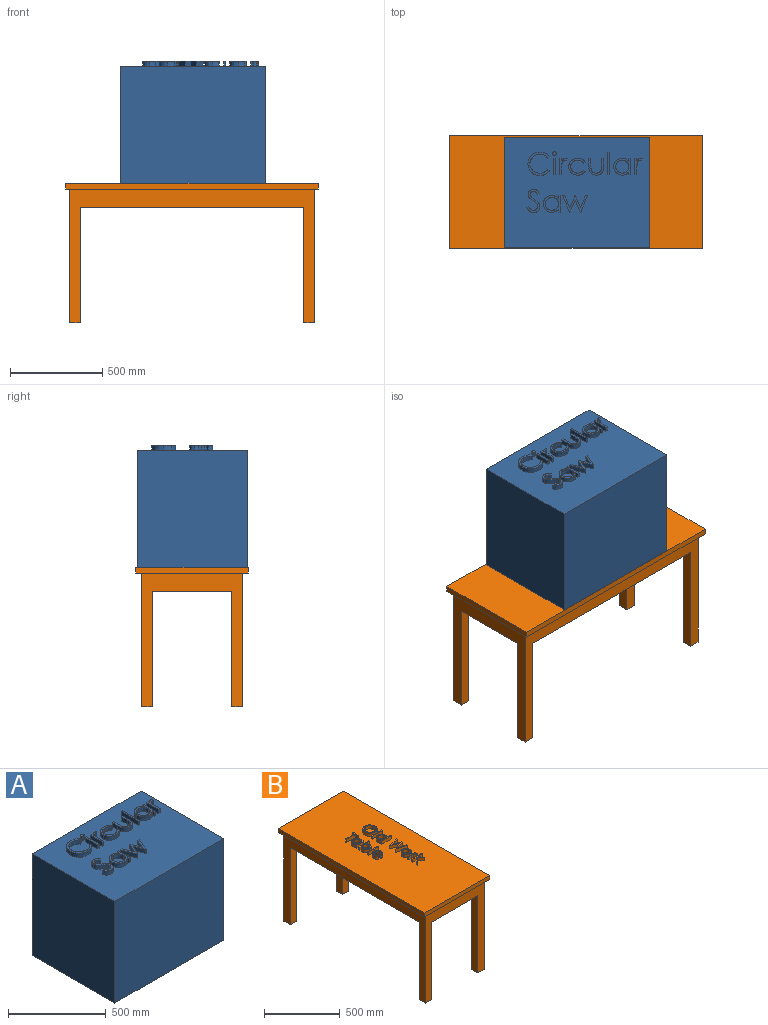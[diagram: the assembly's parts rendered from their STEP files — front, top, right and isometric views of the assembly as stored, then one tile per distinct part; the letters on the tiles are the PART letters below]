
ASSEMBLY  parts=2 mates=1
PART A: 143 faces, bbox 787.4x596.9x660.4 mm
  f0: plane 787.4x596.9mm, normal (0,0,1), area 436057.9mm2, adj f1,f2,f3,f4,f6,f7,f8,f9
  f1: plane 635x596.9mm, normal (-1,0,0), area 379031.5mm2, adj f0,f2,f4,f5
  f2: plane 787.4x635mm, normal (0,-1,0), area 499999mm2, adj f0,f1,f3,f5
  f3: plane 635x596.9mm, normal (1,0,0), area 379031.5mm2, adj f0,f2,f4,f5
  f4: plane 787.4x635mm, normal (0,1,0), area 499999mm2, adj f0,f1,f3,f5
  f5: plane 787.4x596.9mm, normal (0,0,-1), area 469999.1mm2, adj f1,f2,f3,f4
  f6: extruded ~52.64x25.4mm, area 1541mm2, adj f0,f7,f16,f17
  f7: extruded ~64.92x62.72mm, area 2561.4mm2, adj f0,f6,f8,f17
  f8: extruded ~43.02x25.4mm, area 1185.6mm2, adj f0,f7,f9,f17
  f9: extruded ~49.76x25.4mm, area 1419.2mm2, adj f0,f8,f10,f17
  f10: extruded ~52.49x25.4mm, area 1537.6mm2, adj f0,f9,f11,f17
  f11: plane 25.4x9.47mm, normal (0.6,0.8,0), area 301.9mm2, adj f0,f10,f12,f17
  f12: extruded ~43.09x25.4mm, area 1248.8mm2, adj f0,f11,f13,f17
  f13: extruded ~54.16x50.92mm, area 2112.1mm2, adj f0,f12,f14,f17
  f14: extruded ~53.41x51.17mm, area 2096.1mm2, adj f0,f13,f15,f17
  f15: extruded ~43.84x25.4mm, area 1268.5mm2, adj f0,f14,f16,f17
  f16: plane 25.4x9.47mm, normal (0.61,-0.79,0), area 303mm2, adj f0,f6,f15,f17
  f17: plane 126.84x117.56mm, normal (0,0,1), area 3542.4mm2, adj f6,f7,f8,f9,f10,f11,f12,f13
  f18: extruded ~25.4x10.01mm, area 386mm2, adj f0,f19,f21,f22
  f19: extruded ~25.4x10.01mm, area 383.7mm2, adj f0,f18,f20,f22
  f20: extruded ~25.4x10.1mm, area 385.9mm2, adj f0,f19,f21,f22
  f21: extruded ~25.4x10.1mm, area 388.2mm2, adj f0,f18,f20,f22
  f22: plane 20.11x18.56mm, normal (0,0,1), area 293.2mm2, adj f18,f19,f20,f21
  f23: plane 88.17x25.4mm, normal (-1,0,0), area 2239.4mm2, adj f0,f24,f26,f27
  f24: plane 25.4x10.83mm, normal (0,-1,0), area 275mm2, adj f0,f23,f25,f27
  f25: plane 88.17x25.4mm, normal (1,0,0), area 2239.4mm2, adj f0,f24,f26,f27
  f26: plane 25.4x10.83mm, normal (0,1,0), area 275mm2, adj f0,f23,f25,f27
  f27: plane 88.17x10.83mm, normal (0,0,1), area 954.6mm2, adj f23,f24,f25,f26
  f28: plane 88.17x25.4mm, normal (-1,0,0), area 2239.4mm2, adj f0,f29,f38,f39
  f29: plane 25.4x10.83mm, normal (0,-1,0), area 275mm2, adj f0,f28,f30,f39
  f30: plane 29.63x25.4mm, normal (1,0,0), area 752.6mm2, adj f0,f29,f31,f39
  f31: extruded ~30.26x25.4mm, area 771.6mm2, adj f0,f30,f32,f39
  f32: extruded ~25.4x19mm, area 705.1mm2, adj f0,f31,f33,f39
  f33: extruded ~25.4x5.53mm, area 147.3mm2, adj f0,f32,f34,f39
  f34: plane 25.4x9.38mm, normal (0.84,-0.54,0), area 282mm2, adj f0,f33,f35,f39
  f35: extruded ~25.4x9.43mm, area 254.5mm2, adj f0,f34,f36,f39
  f36: extruded ~25.4x21.51mm, area 689.8mm2, adj f0,f35,f37,f39
  f37: plane 25.4x12.98mm, normal (1,0,0), area 329.7mm2, adj f0,f36,f38,f39
  f38: plane 25.4x10.83mm, normal (0,1,0), area 275mm2, adj f0,f28,f37,f39
  f39: plane 89.71x41.76mm, normal (0,0,1), area 1310.5mm2, adj f28,f29,f30,f31,f32,f33,f34,f35
  f40: extruded ~40.36x25.4mm, area 1205.3mm2, adj f0,f41,f49,f50
  f41: extruded ~49.35x46.36mm, area 1919.1mm2, adj f0,f40,f42,f50
  f42: extruded ~48.46x44.91mm, area 1873mm2, adj f0,f41,f43,f50
  f43: extruded ~41.26x25.4mm, area 1219.7mm2, adj f0,f42,f44,f50
  f44: plane 25.4x9.06mm, normal (0.55,0.84,0), area 275.3mm2, adj f0,f43,f45,f50
  f45: extruded ~32.02x25.4mm, area 936.8mm2, adj f0,f44,f46,f50
  f46: extruded ~37.8x35.04mm, area 1460.5mm2, adj f0,f45,f47,f50
  f47: extruded ~37.73x34.56mm, area 1450mm2, adj f0,f46,f48,f50
  f48: extruded ~32.1x25.4mm, area 940.7mm2, adj f0,f47,f49,f50
  f49: plane 25.4x9.06mm, normal (0.53,-0.85,0), area 271mm2, adj f0,f40,f48,f50
  f50: plane 91.26x89.71mm, normal (0,0,1), area 2367.7mm2, adj f40,f41,f42,f43,f44,f45,f46,f47
  f51: plane 42.13x25.4mm, normal (-1,0,0), area 1070mm2, adj f0,f52,f62,f63
  f52: extruded ~47.59x39.52mm, area 1809.1mm2, adj f0,f51,f53,f63
  f53: extruded ~46.79x39.37mm, area 1786.7mm2, adj f0,f52,f54,f63
  f54: plane 42.92x25.4mm, normal (1,0,0), area 1090.3mm2, adj f0,f53,f55,f63
  f55: plane 25.4x10.83mm, normal (0,1,0), area 275mm2, adj f0,f54,f56,f63
  f56: plane 40.89x25.4mm, normal (-1,0,0), area 1038.7mm2, adj f0,f55,f57,f63
  f57: extruded ~25.4x21.49mm, area 549.3mm2, adj f0,f56,f58,f63
  f58: extruded ~26.66x25.4mm, area 851.2mm2, adj f0,f57,f59,f63
  f59: extruded ~27.07x25.4mm, area 877.1mm2, adj f0,f58,f60,f63
  f60: extruded ~25.4x20.62mm, area 526.9mm2, adj f0,f59,f61,f63
  f61: plane 40.89x25.4mm, normal (1,0,0), area 1038.7mm2, adj f0,f60,f62,f63
  f62: plane 25.4x10.83mm, normal (0,1,0), area 275mm2, adj f0,f51,f61,f63
  f63: plane 89.71x78.89mm, normal (0,0,1), area 2277.8mm2, adj f51,f52,f53,f54,f55,f56,f57,f58
  f64: plane 123.74x25.4mm, normal (-1,0,0), area 3143.1mm2, adj f0,f65,f67,f68
  f65: plane 25.4x10.83mm, normal (0,-1,0), area 275mm2, adj f0,f64,f66,f68
  f66: plane 123.74x25.4mm, normal (1,0,0), area 3143.1mm2, adj f0,f65,f67,f68
  f67: plane 25.4x10.83mm, normal (0,1,0), area 275mm2, adj f0,f64,f66,f68
  f68: plane 123.74x10.83mm, normal (0,0,1), area 1339.8mm2, adj f64,f65,f66,f67
  f69: plane 92.81x91.26mm, normal (0,0,1), area 3273.7mm2, adj f70,f71,f72,f73,f74,f75,f76,f77
  f70: plane 25.4x10.83mm, normal (0,1,0), area 275mm2, adj f0,f69,f71,f78
  f71: plane 25.4x16.31mm, normal (-1,0,0), area 414.4mm2, adj f0,f69,f70,f72
  f72: extruded ~35.67x25.4mm, area 1056mm2, adj f0,f69,f71,f73
  f73: extruded ~46.31x45.39mm, area 1831.7mm2, adj f0,f69,f72,f74
  f74: extruded ~45.97x45.87mm, area 1836.2mm2, adj f0,f69,f73,f75
  f75: extruded ~36.01x25.4mm, area 1045.3mm2, adj f0,f69,f74,f76
  f76: plane 25.4x15.25mm, normal (-1,0,0), area 387.4mm2, adj f0,f69,f75,f77
  f77: plane 25.4x10.83mm, normal (0,-1,0), area 275mm2, adj f0,f69,f76,f78
  f78: plane 88.17x25.4mm, normal (1,0,0), area 2239.4mm2, adj f0,f69,f70,f77
  f79: extruded ~35.53x35mm, area 1414.4mm2, adj f69,f80,f82,f83
  f80: extruded ~35.62x34.68mm, area 1404mm2, adj f69,f79,f81,f83
  f81: extruded ~35.53x34.92mm, area 1403.8mm2, adj f69,f80,f82,f83
  f82: extruded ~35.62x34.61mm, area 1408mm2, adj f69,f79,f81,f83
  f83: plane 71.15x69.61mm, normal (0,0,1), area 3908.6mm2, adj f79,f80,f81,f82
  f84: plane 88.17x25.4mm, normal (-1,0,0), area 2239.4mm2, adj f0,f85,f94,f95
  f85: plane 25.4x10.83mm, normal (0,-1,0), area 275mm2, adj f0,f84,f86,f95
  f86: plane 29.63x25.4mm, normal (1,0,0), area 752.6mm2, adj f0,f85,f87,f95
  f87: extruded ~30.26x25.4mm, area 771.6mm2, adj f0,f86,f88,f95
  f88: extruded ~25.4x19mm, area 705.1mm2, adj f0,f87,f89,f95
  f89: extruded ~25.4x5.53mm, area 147.3mm2, adj f0,f88,f90,f95
  f90: plane 25.4x9.38mm, normal (0.84,-0.54,0), area 282mm2, adj f0,f89,f91,f95
  f91: extruded ~25.4x9.43mm, area 254.5mm2, adj f0,f90,f92,f95
  f92: extruded ~25.4x21.51mm, area 689.8mm2, adj f0,f91,f93,f95
  f93: plane 25.4x12.98mm, normal (1,0,0), area 329.7mm2, adj f0,f92,f94,f95
  f94: plane 25.4x10.83mm, normal (0,1,0), area 275mm2, adj f0,f84,f93,f95
  f95: plane 89.71x41.76mm, normal (0,0,1), area 1310.5mm2, adj f84,f85,f86,f87,f88,f89,f90,f91
  f96: extruded ~36.69x26.37mm, area 1213.6mm2, adj f0,f97,f112,f113
  f97: extruded ~34.46x32.65mm, area 1339.8mm2, adj f0,f96,f98,f113
  f98: extruded ~38.94x28.42mm, area 1272.9mm2, adj f0,f97,f99,f113
  f99: extruded ~25.4x16.22mm, area 512.8mm2, adj f0,f98,f100,f113
  f100: extruded ~25.4x15.59mm, area 458.5mm2, adj f0,f99,f101,f113
  f101: extruded ~25.4x17.69mm, area 663.4mm2, adj f0,f100,f102,f113
  f102: extruded ~25.4x23.56mm, area 746.1mm2, adj f0,f101,f103,f113
  f103: plane 25.4x9.79mm, normal (0.6,-0.8,0), area 312mm2, adj f0,f102,f104,f113
  f104: extruded ~32.14x25.4mm, area 1009.9mm2, adj f0,f103,f105,f113
  f105: extruded ~29.73x28.16mm, area 1160.8mm2, adj f0,f104,f106,f113
  f106: extruded ~25.4x18.37mm, area 506.9mm2, adj f0,f105,f107,f113
  f107: extruded ~25.4x19.77mm, area 654.2mm2, adj f0,f106,f108,f113
  f108: extruded ~25.4x21.75mm, area 740.2mm2, adj f0,f107,f109,f113
  f109: extruded ~25.4x11.84mm, area 325.9mm2, adj f0,f108,f110,f113
  f110: extruded ~25.4x23.64mm, area 883mm2, adj f0,f109,f111,f113
  f111: extruded ~26.49x25.4mm, area 886.6mm2, adj f0,f110,f112,f113
  f112: plane 25.4x10.2mm, normal (-0.51,0.86,0), area 302mm2, adj f0,f96,f111,f113
  f113: plane 126.84x71.15mm, normal (0,0,1), area 2836.1mm2, adj f96,f97,f98,f99,f100,f101,f102,f103
  f114: plane 92.81x91.26mm, normal (0,0,1), area 3273.6mm2, adj f115,f116,f117,f118,f119,f120,f121,f122
  f115: plane 25.4x10.83mm, normal (0,1,0), area 275mm2, adj f0,f114,f116,f123
  f116: plane 25.4x16.31mm, normal (-1,0,0), area 414.4mm2, adj f0,f114,f115,f117
  f117: extruded ~35.67x25.4mm, area 1056mm2, adj f0,f114,f116,f118
  f118: extruded ~46.31x45.39mm, area 1831.7mm2, adj f0,f114,f117,f119
  f119: extruded ~45.97x45.87mm, area 1836.2mm2, adj f0,f114,f118,f120
  f120: extruded ~36.01x25.4mm, area 1045.3mm2, adj f0,f114,f119,f121
  f121: plane 25.4x15.25mm, normal (-1,0,0), area 387.4mm2, adj f0,f114,f120,f122
  f122: plane 25.4x10.83mm, normal (0,-1,0), area 275mm2, adj f0,f114,f121,f123
  f123: plane 88.17x25.4mm, normal (1,0,0), area 2239.4mm2, adj f0,f114,f115,f122
  f124: extruded ~35.53x35mm, area 1414.4mm2, adj f114,f125,f127,f128
  f125: extruded ~35.62x34.68mm, area 1404mm2, adj f114,f124,f126,f128
  f126: extruded ~35.53x34.92mm, area 1403.8mm2, adj f114,f125,f127,f128
  f127: extruded ~35.62x34.61mm, area 1408mm2, adj f114,f124,f126,f128
  f128: plane 71.15x69.61mm, normal (0,0,1), area 3908.6mm2, adj f124,f125,f126,f127
  f129: plane 88.17x36.52mm, normal (-0.92,-0.38,0), area 2424mm2, adj f0,f130,f141,f142
  f130: plane 25.4x2.01mm, normal (0,-1,0), area 51mm2, adj f0,f129,f131,f142
  f131: plane 63.42x28.76mm, normal (0.91,-0.41,0), area 1768.7mm2, adj f0,f130,f132,f142
  f132: plane 63.42x28.18mm, normal (-0.91,-0.41,0), area 1762.7mm2, adj f0,f131,f133,f142
  f133: plane 25.4x2.25mm, normal (0,-1,0), area 57.1mm2, adj f0,f132,f134,f142
  f134: plane 88.17x36.86mm, normal (0.92,-0.39,0), area 2427.3mm2, adj f0,f133,f135,f142
  f135: plane 25.4x11.38mm, normal (0,1,0), area 289.1mm2, adj f0,f134,f136,f142
  f136: plane 63.42x26.51mm, normal (-0.92,0.39,0), area 1745.9mm2, adj f0,f135,f137,f142
  f137: plane 63.42x28.16mm, normal (0.91,0.41,0), area 1762.5mm2, adj f0,f136,f138,f142
  f138: plane 25.4x1.84mm, normal (0,1,0), area 46.7mm2, adj f0,f137,f139,f142
  f139: plane 63.42x28.79mm, normal (-0.91,0.41,0), area 1769mm2, adj f0,f138,f140,f142
  f140: plane 63.42x26.27mm, normal (0.92,0.38,0), area 1743.6mm2, adj f0,f139,f141,f142
  f141: plane 25.4x11.63mm, normal (0,1,0), area 295.3mm2, adj f0,f129,f140,f142
  f142: plane 134.57x88.17mm, normal (0,0,1), area 3345.2mm2, adj f129,f130,f131,f132,f133,f134,f135,f136
PART B: 163 faces, bbox 609.9x1371.7x781.1 mm
  f0: plane 1371.73x609.89mm, normal (0,0,1), area 803903mm2, adj f10,f11,f12,f13,f24,f25,f26,f27
  f1: plane 1371.73x609.89mm, normal (0,0,-1), area 111370.7mm2, adj f10,f11,f12,f13,f14,f15,f17,f19
  f2: plane 625.48x57.15mm, normal (1,0,0), area 35745.9mm2, adj f3,f14,f16,f22
  f3: plane 625.48x57.15mm, normal (0,-1,0), area 35745.9mm2, adj f2,f15,f16,f22
  f4: plane 625.48x57.15mm, normal (0,-1,0), area 35745.9mm2, adj f5,f17,f18,f22
  f5: plane 625.48x57.15mm, normal (-1,0,0), area 35745.9mm2, adj f4,f14,f18,f22
  f6: plane 625.48x57.15mm, normal (-1,0,0), area 35745.9mm2, adj f7,f19,f20,f22
  f7: plane 625.48x57.15mm, normal (0,1,0), area 35745.9mm2, adj f6,f17,f20,f22
  f8: plane 625.48x57.15mm, normal (0,1,0), area 35745.9mm2, adj f9,f15,f21,f22
  f9: plane 625.48x57.15mm, normal (1,0,0), area 35745.9mm2, adj f8,f19,f21,f22
  f10: plane 609.6x31.75mm, normal (0,1,0), area 19354.8mm2, adj f0,f1,f11,f13
  f11: plane 1371.6x31.75mm, normal (-1,0,0), area 43548.3mm2, adj f0,f1,f10,f12
  f12: plane 609.6x31.75mm, normal (0,-1,0), area 19354.8mm2, adj f0,f1,f11,f13
  f13: plane 1371.6x31.75mm, normal (1,0,0), area 43548.3mm2, adj f0,f1,f10,f12
  f14: plane 723.9x546.1mm, normal (0,1,0), area 125241.7mm2, adj f1,f2,f5,f15,f16,f17,f18,f22
  f15: plane 1327.15x723.9mm, normal (-1,0,0), area 202116.5mm2, adj f1,f3,f8,f14,f16,f19,f21,f22
  f16: plane 57.16x57.16mm, normal (0,0,-1), area 3266.1mm2, adj f2,f3,f14,f15
  f17: plane 1327.15x723.9mm, normal (1,0,0), area 202116.5mm2, adj f1,f4,f7,f14,f18,f19,f20,f22
  f18: plane 57.16x57.16mm, normal (0,0,-1), area 3266.1mm2, adj f4,f5,f14,f17
  f19: plane 723.9x546.1mm, normal (0,-1,0), area 125241.7mm2, adj f1,f6,f9,f15,f17,f20,f21,f22
  f20: plane 57.16x57.16mm, normal (0,0,-1), area 3266.1mm2, adj f6,f7,f17,f19
  f21: plane 57.16x57.16mm, normal (0,0,-1), area 3266.1mm2, adj f8,f9,f15,f19
  f22: plane 1327.24x546.36mm, normal (0,0,-1), area 711692.1mm2, adj f2,f3,f4,f5,f6,f7,f8,f9
  f23: plane 93.46x93.46mm, normal (0,0,1), area 2301.1mm2, adj f24,f25,f26,f27,f28,f29,f30,f31
  f24: extruded ~47.13x46.15mm, area 1864.4mm2, adj f0,f23,f25,f27
  f25: extruded ~46.88x46.33mm, area 1865mm2, adj f0,f23,f24,f26
  f26: extruded ~46.78x46.58mm, area 1868mm2, adj f0,f23,f25,f27
  f27: extruded ~47.31x46.68mm, area 1884.7mm2, adj f0,f23,f24,f26
  f28: extruded ~38.94x37.55mm, area 1529.2mm2, adj f23,f29,f31,f32
  f29: extruded ~38.57x37.98mm, area 1529.4mm2, adj f23,f28,f30,f32
  f30: extruded ~38.58x37.25mm, area 1516.9mm2, adj f23,f29,f31,f32
  f31: extruded ~38.92x37.67mm, area 1535.2mm2, adj f23,f28,f30,f32
  f32: plane 77.5x75.22mm, normal (0,0,1), area 4603.4mm2, adj f28,f29,f30,f31
  f33: plane 91.18x25.4mm, normal (0,1,0), area 2316mm2, adj f0,f34,f36,f37
  f34: plane 25.4x7.98mm, normal (-1,0,0), area 202.6mm2, adj f0,f33,f35,f37
  f35: plane 91.18x25.4mm, normal (0,-1,0), area 2316mm2, adj f0,f34,f36,f37
  f36: plane 25.4x7.98mm, normal (1,0,0), area 202.6mm2, adj f0,f33,f35,f37
  f37: plane 91.18x8mm, normal (0,0,1), area 727.4mm2, adj f33,f34,f35,f36
  f38: plane 92.33x68.39mm, normal (0,0,1), area 1979.8mm2, adj f39,f40,f41,f42,f43,f44,f45,f46
  f39: plane 25.4x7.98mm, normal (1,0,0), area 202.6mm2, adj f0,f38,f40,f47
  f40: plane 38.79x25.4mm, normal (0,1,0), area 985.2mm2, adj f0,f38,f39,f41
  f41: extruded ~26.29x25.4mm, area 784.2mm2, adj f0,f38,f40,f42
  f42: extruded ~34.11x33.45mm, area 1349.6mm2, adj f0,f38,f41,f43
  f43: extruded ~33.88x33.79mm, area 1353mm2, adj f0,f38,f42,f44
  f44: extruded ~26.53x25.4mm, area 770.2mm2, adj f0,f38,f43,f45
  f45: plane 25.4x11.24mm, normal (0,1,0), area 285.4mm2, adj f0,f38,f44,f46
  f46: plane 25.4x7.98mm, normal (-1,0,0), area 202.6mm2, adj f0,f38,f45,f47
  f47: plane 91.18x25.4mm, normal (0,-1,0), area 2316mm2, adj f0,f38,f39,f46
  f48: extruded ~26.18x25.78mm, area 1042.2mm2, adj f38,f49,f51,f52
  f49: extruded ~26.24x25.56mm, area 1034.5mm2, adj f38,f48,f50,f52
  f50: extruded ~26.18x25.73mm, area 1034.4mm2, adj f38,f49,f51,f52
  f51: extruded ~26.24x25.51mm, area 1037.5mm2, adj f38,f48,f50,f52
  f52: plane 52.43x51.29mm, normal (0,0,1), area 2122.1mm2, adj f48,f49,f50,f51
  f53: plane 88.9x25.4mm, normal (-0.26,0.97,0), area 2336.6mm2, adj f0,f54,f65,f66
  f54: plane 25.4x1.14mm, normal (-1,0,0), area 28.9mm2, adj f0,f53,f55,f66
  f55: plane 68x27.05mm, normal (-0.37,-0.93,0), area 1858.8mm2, adj f0,f54,f56,f66
  f56: plane 67.99x26.76mm, normal (-0.37,0.93,0), area 1855.9mm2, adj f0,f55,f57,f66
  f57: plane 25.4x1.14mm, normal (-1,0,0), area 28.9mm2, adj f0,f56,f58,f66
  f58: plane 88.91x25.4mm, normal (-0.26,-0.97,0), area 2338.7mm2, adj f0,f57,f59,f66
  f59: plane 25.4x8.16mm, normal (1,0,0), area 207.2mm2, adj f0,f58,f60,f66
  f60: plane 64.76x25.4mm, normal (0.26,0.97,0), area 1703.6mm2, adj f0,f59,f61,f66
  f61: plane 64.75x25.41mm, normal (0.37,-0.93,0), area 1766.7mm2, adj f0,f60,f62,f66
  f62: plane 25.4x1.16mm, normal (1,0,0), area 29.4mm2, adj f0,f61,f63,f66
  f63: plane 65.2x25.86mm, normal (0.37,0.93,0), area 1781.7mm2, adj f0,f62,f64,f66
  f64: plane 65.19x25.4mm, normal (0.26,-0.97,0), area 1714mm2, adj f0,f63,f65,f66
  f65: plane 25.4x8.25mm, normal (1,0,0), area 209.4mm2, adj f0,f53,f64,f66
  f66: plane 103.72x88.92mm, normal (0,0,1), area 2475.1mm2, adj f53,f54,f55,f56,f57,f58,f59,f60
  f67: plane 67.25x67.25mm, normal (0,0,1), area 1502.1mm2, adj f68,f69,f70,f71,f72,f73,f74,f75
  f68: extruded ~25.4x24.75mm, area 707.2mm2, adj f0,f67,f69,f73
  f69: extruded ~25.4x23.05mm, area 642.9mm2, adj f0,f67,f68,f70
  f70: extruded ~33.67x33.44mm, area 1344.2mm2, adj f0,f67,f69,f71
  f71: extruded ~33.58x33.45mm, area 1342.5mm2, adj f0,f67,f70,f72
  f72: extruded ~25.4x23.1mm, area 644.2mm2, adj f0,f67,f71,f73
  f73: extruded ~25.4x24.69mm, area 704.8mm2, adj f0,f67,f68,f72
  f74: extruded ~25.87x25.65mm, area 1028.6mm2, adj f67,f75,f77,f78
  f75: extruded ~25.88x25.64mm, area 1028.9mm2, adj f67,f74,f76,f78
  f76: extruded ~25.65x25.41mm, area 1022.3mm2, adj f67,f75,f77,f78
  f77: extruded ~25.64x25.42mm, area 1022.2mm2, adj f67,f74,f76,f78
  f78: plane 51.29x51.29mm, normal (0,0,1), area 2075.1mm2, adj f74,f75,f76,f77
  f79: plane 64.97x25.4mm, normal (0,1,0), area 1650.1mm2, adj f0,f80,f89,f90
  f80: plane 25.4x7.98mm, normal (-1,0,0), area 202.6mm2, adj f0,f79,f81,f90
  f81: plane 25.4x21.83mm, normal (0,-1,0), area 554.6mm2, adj f0,f80,f82,f90
  f82: extruded ~25.4x22.3mm, area 568.5mm2, adj f0,f81,f83,f90
  f83: extruded ~25.4x14mm, area 519.5mm2, adj f0,f82,f84,f90
  f84: extruded ~25.4x4.08mm, area 108.5mm2, adj f0,f83,f85,f90
  f85: plane 25.4x6.91mm, normal (-0.54,-0.84,0), area 207.8mm2, adj f0,f84,f86,f90
  f86: extruded ~25.4x6.95mm, area 187.5mm2, adj f0,f85,f87,f90
  f87: extruded ~25.4x15.85mm, area 508.3mm2, adj f0,f86,f88,f90
  f88: plane 25.4x9.56mm, normal (0,-1,0), area 242.9mm2, adj f0,f87,f89,f90
  f89: plane 25.4x7.98mm, normal (1,0,0), area 202.6mm2, adj f0,f79,f88,f90
  f90: plane 66.11x30.77mm, normal (0,0,1), area 711.5mm2, adj f79,f80,f81,f82,f83,f84,f85,f86
  f91: plane 91.18x25.4mm, normal (0,1,0), area 2316mm2, adj f0,f92,f101,f102
  f92: plane 25.4x7.98mm, normal (-1,0,0), area 202.6mm2, adj f0,f91,f93,f102
  f93: plane 29.94x25.4mm, normal (0,-1,0), area 760.4mm2, adj f0,f92,f94,f102
  f94: plane 33.01x29.93mm, normal (-0.74,0.67,0), area 1131.7mm2, adj f0,f93,f95,f102
  f95: plane 25.4x11.45mm, normal (-1,0,0), area 290.9mm2, adj f0,f94,f96,f102
  f96: plane 37.73x34.18mm, normal (0.74,-0.67,0), area 1293.1mm2, adj f0,f95,f97,f102
  f97: plane 34.29x30.78mm, normal (-0.74,-0.67,0), area 1170.4mm2, adj f0,f96,f98,f102
  f98: plane 25.4x11.47mm, normal (1,0,0), area 291.3mm2, adj f0,f97,f99,f102
  f99: plane 29.56x26.51mm, normal (0.74,0.67,0), area 1008.4mm2, adj f0,f98,f100,f102
  f100: plane 52.71x25.4mm, normal (0,-1,0), area 1338.9mm2, adj f0,f99,f101,f102
  f101: plane 25.4x7.98mm, normal (1,0,0), area 202.6mm2, adj f0,f91,f100,f102
  f102: plane 91.18x52.45mm, normal (0,0,1), area 1451.7mm2, adj f91,f92,f93,f94,f95,f96,f97,f98
  f103: plane 25.4x19.38mm, normal (-1,0,0), area 492.1mm2, adj f0,f104,f110,f111
  f104: plane 79.78x25.4mm, normal (0,1,0), area 2026.5mm2, adj f0,f103,f105,f111
  f105: plane 25.4x7.98mm, normal (-1,0,0), area 202.6mm2, adj f0,f104,f106,f111
  f106: plane 79.78x25.4mm, normal (0,-1,0), area 2026.5mm2, adj f0,f105,f107,f111
  f107: plane 25.4x19.38mm, normal (-1,0,0), area 492.1mm2, adj f0,f106,f108,f111
  f108: plane 25.4x9.12mm, normal (0,-1,0), area 231.6mm2, adj f0,f107,f109,f111
  f109: plane 46.73x25.4mm, normal (1,0,0), area 1186.9mm2, adj f0,f108,f110,f111
  f110: plane 25.4x9.12mm, normal (0,1,0), area 231.6mm2, adj f0,f103,f109,f111
  f111: plane 88.91x46.73mm, normal (0,0,1), area 1062.6mm2, adj f103,f104,f105,f106,f107,f108,f109,f110
  f112: plane 68.39x67.25mm, normal (0,0,1), area 1777.4mm2, adj f113,f114,f115,f116,f117,f118,f119,f120
  f113: plane 25.4x7.98mm, normal (1,0,0), area 202.6mm2, adj f0,f112,f114,f121
  f114: plane 25.4x12.02mm, normal (0,1,0), area 305.3mm2, adj f0,f112,f113,f115
  f115: extruded ~26.29x25.4mm, area 778.1mm2, adj f0,f112,f114,f116
  f116: extruded ~34.11x33.45mm, area 1349.6mm2, adj f0,f112,f115,f117
  f117: extruded ~33.88x33.79mm, area 1353mm2, adj f0,f112,f116,f118
  f118: extruded ~26.53x25.4mm, area 770.2mm2, adj f0,f112,f117,f119
  f119: plane 25.4x11.24mm, normal (0,1,0), area 285.4mm2, adj f0,f112,f118,f120
  f120: plane 25.4x7.98mm, normal (-1,0,0), area 202.6mm2, adj f0,f112,f119,f121
  f121: plane 64.97x25.4mm, normal (0,-1,0), area 1650.1mm2, adj f0,f112,f113,f120
  f122: extruded ~26.18x25.78mm, area 1042.2mm2, adj f112,f123,f125,f126
  f123: extruded ~26.24x25.56mm, area 1034.5mm2, adj f112,f122,f124,f126
  f124: extruded ~26.18x25.73mm, area 1034.4mm2, adj f112,f123,f125,f126
  f125: extruded ~26.24x25.51mm, area 1037.5mm2, adj f112,f122,f124,f126
  f126: plane 52.43x51.29mm, normal (0,0,1), area 2122.1mm2, adj f122,f123,f124,f125
  f127: plane 92.31x68.4mm, normal (0,0,1), area 1980.4mm2, adj f128,f129,f130,f131,f132,f133,f134,f135
  f128: plane 25.4x7.98mm, normal (-1,0,0), area 202.6mm2, adj f0,f127,f129,f136
  f129: plane 25.4x12.02mm, normal (0,-1,0), area 305.3mm2, adj f0,f127,f128,f130
  f130: extruded ~26.25x25.4mm, area 776.9mm2, adj f0,f127,f129,f131
  f131: extruded ~34.15x33.51mm, area 1351.6mm2, adj f0,f127,f130,f132
  f132: extruded ~33.91x33.74mm, area 1352.4mm2, adj f0,f127,f131,f133
  f133: extruded ~26.5x25.4mm, area 775.8mm2, adj f0,f127,f132,f134
  f134: plane 38x25.4mm, normal (0,-1,0), area 965.3mm2, adj f0,f127,f133,f135
  f135: plane 25.4x7.98mm, normal (1,0,0), area 202.6mm2, adj f0,f127,f134,f136
  f136: plane 91.18x25.4mm, normal (0,1,0), area 2316mm2, adj f0,f127,f128,f135
  f137: extruded ~26.18x25.76mm, area 1042mm2, adj f127,f138,f140,f141
  f138: extruded ~26.24x25.53mm, area 1033.6mm2, adj f127,f137,f139,f141
  f139: extruded ~26.13x25.76mm, area 1033.9mm2, adj f127,f138,f140,f141
  f140: extruded ~26.3x25.53mm, area 1038.3mm2, adj f127,f137,f139,f141
  f141: plane 52.43x51.29mm, normal (0,0,1), area 2121.3mm2, adj f137,f138,f139,f140
  f142: plane 91.18x25.4mm, normal (0,1,0), area 2316mm2, adj f0,f143,f145,f146
  f143: plane 25.4x7.98mm, normal (-1,0,0), area 202.6mm2, adj f0,f142,f144,f146
  f144: plane 91.18x25.4mm, normal (0,-1,0), area 2316mm2, adj f0,f143,f145,f146
  f145: plane 25.4x7.98mm, normal (1,0,0), area 202.6mm2, adj f0,f142,f144,f146
  f146: plane 91.18x8mm, normal (0,0,1), area 727.4mm2, adj f142,f143,f144,f145
  f147: plane 67.25x66.11mm, normal (0,0,1), area 1764.3mm2, adj f148,f149,f150,f151,f152,f153,f154,f155
  f148: extruded ~25.4x23.91mm, area 734.6mm2, adj f0,f147,f149,f157
  f149: extruded ~25.4x23.93mm, area 954.7mm2, adj f0,f147,f148,f150
  f150: plane 58.13x25.4mm, normal (-1,0,0), area 1476.4mm2, adj f0,f147,f149,f151
  f151: extruded ~25.4x22.54mm, area 611.1mm2, adj f0,f147,f150,f152
  f152: extruded ~26.16x25.4mm, area 768.7mm2, adj f0,f147,f151,f153
  f153: extruded ~25.4x25.39mm, area 741.9mm2, adj f0,f147,f152,f154
  f154: extruded ~25.4x21.69mm, area 594.2mm2, adj f0,f147,f153,f155
  f155: extruded ~33.44x32.69mm, area 1328.8mm2, adj f0,f147,f154,f156
  f156: extruded ~30x25.4mm, area 938.4mm2, adj f0,f147,f155,f157
  f157: plane 25.4x7.09mm, normal (0.89,-0.46,0), area 203.3mm2, adj f0,f147,f148,f156
  f158: plane 49.31x25.4mm, normal (1,0,0), area 1252.5mm2, adj f147,f159,f161,f162
  f159: extruded ~25.4x24.85mm, area 868.8mm2, adj f147,f158,f160,f162
  f160: extruded ~25.4x16.74mm, area 462.8mm2, adj f147,f159,f161,f162
  f161: extruded ~25.4x13.29mm, area 395.8mm2, adj f147,f158,f160,f162
  f162: plane 49.31x19.38mm, normal (0,0,1), area 719.5mm2, adj f158,f159,f160,f161
PLACE A t=(-918.03,856.71,1393.47)mm
PLACE B rot(axis=(0,0,1),90deg) t=(521.14,-5437.28,1393.47)mm
MATE fastened A.f5 <-> B.f0  axis (0,0,-1) through (1154.65,-3920.13,-164.05)mm
